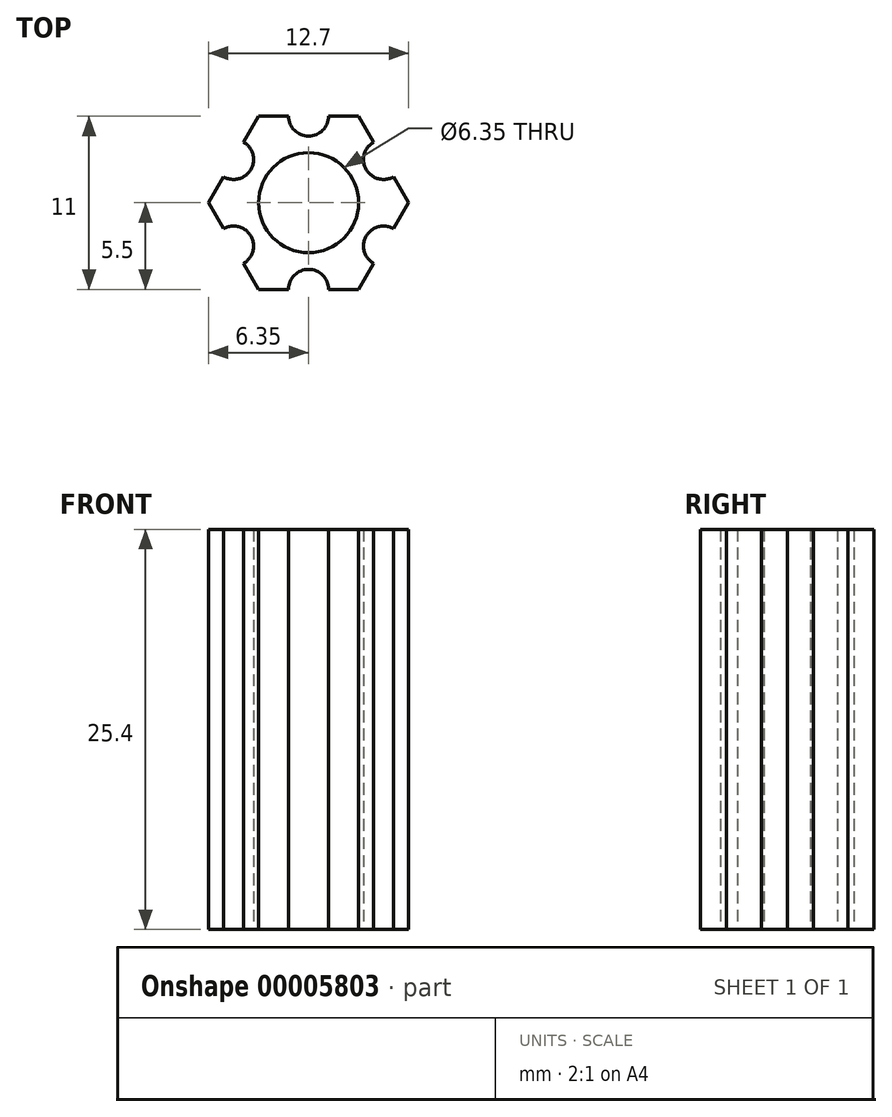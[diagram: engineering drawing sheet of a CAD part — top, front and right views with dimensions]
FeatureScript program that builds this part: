
annotation { "Feature Type Name" : "Feature", "Feature Type Description" : "" }
export const myFeature = defineFeature(function(context is Context, id is Id, definition is map)
    precondition{}
    {
        {
            var Q0;
            Q0=qCreatedBy(makeId("Top.planeOp"),FACE);
            var sketch = newSketch(context, id + "F0", { "sketchPlane" : qUnion([Q0])});
            skCircle(sketch, "E0.cCircle", {"center": v(0, 0) * mm, "radius": 6.35 * mm, "construction": true});
            skLineSegment(sketch, "E0.0", {"start": v(6.35, 0) * mm, "end": v(5.4, -1.65) * mm});
            skLineSegment(sketch, "E0.1", {"start": v(3.17, -5.5) * mm, "end": v(1.27, -5.5) * mm});
            skLineSegment(sketch, "E0.2", {"start": v(-3.17, -5.5) * mm, "end": v(-4.13, -3.85) * mm});
            skLineSegment(sketch, "E0.3", {"start": v(-6.35, 0) * mm, "end": v(-5.4, 1.65) * mm});
            skLineSegment(sketch, "E0.4", {"start": v(-3.17, 5.5) * mm, "end": v(-1.27, 5.5) * mm});
            skLineSegment(sketch, "E0.5", {"start": v(3.17, 5.5) * mm, "end": v(4.13, 3.85) * mm});
            skArc(sketch, "E1", {"start": v(-5.4, 1.65) * mm, "mid": v(-3.66, 2.11) * mm, "end": v(-4.13, 3.85) * mm});
            skLineSegment(sketch, "E2.trimOffspring", {"start": v(-4.13, 3.85) * mm, "end": v(-3.18, 5.5) * mm});
            skArc(sketch, "E3.2.0", {"start": v(1.27, -5.5) * mm, "mid": v(0, -4.23) * mm, "end": v(-1.27, -5.5) * mm});
            skArc(sketch, "E3.3.0", {"start": v(5.4, -1.65) * mm, "mid": v(3.66, -2.11) * mm, "end": v(4.13, -3.85) * mm});
            skArc(sketch, "E3.4.0", {"start": v(4.13, 3.85) * mm, "mid": v(3.66, 2.11) * mm, "end": v(5.4, 1.65) * mm});
            skArc(sketch, "E3.5.0", {"start": v(-1.27, 5.5) * mm, "mid": v(0, 4.23) * mm, "end": v(1.27, 5.5) * mm});
            skLineSegment(sketch, "E4.trimOffspring", {"start": v(1.27, 5.5) * mm, "end": v(3.17, 5.5) * mm});
            skLineSegment(sketch, "E5.trimOffspring", {"start": v(5.4, 1.65) * mm, "end": v(6.35, 0) * mm});
            skLineSegment(sketch, "E6.trimOffspring", {"start": v(4.13, -3.85) * mm, "end": v(3.18, -5.5) * mm});
            skLineSegment(sketch, "E7.trimOffspring", {"start": v(-1.27, -5.5) * mm, "end": v(-3.17, -5.5) * mm});
            skArc(sketch, "E8", {"start": v(-4.13, -3.85) * mm, "mid": v(-3.66, -2.11) * mm, "end": v(-5.4, -1.65) * mm});
            skLineSegment(sketch, "E9.trimOffspring", {"start": v(-5.4, -1.65) * mm, "end": v(-6.35, 0) * mm});
            skCircle(sketch, "E10", {"center": v(0, 0) * mm, "radius": 3.18 * mm});
            skSolve(sketch);
        }
        {
            var Q0;
            Q0=makeQuery(id+"F0.imprint","IMPRINT",FACE,{"disambiguationData":[TD([[makeQuery(id+"F0.imprint","IMPRINT",EDGE,{"derivedFrom":sQuery(id+"F0.wireOp",EDGE,"E0.0")}),-1.0]])]});
            extrude(context, id + "F1", {"entities" : qUnion([Q0]), "depth" : 25.4 * mm});
        }
    });
